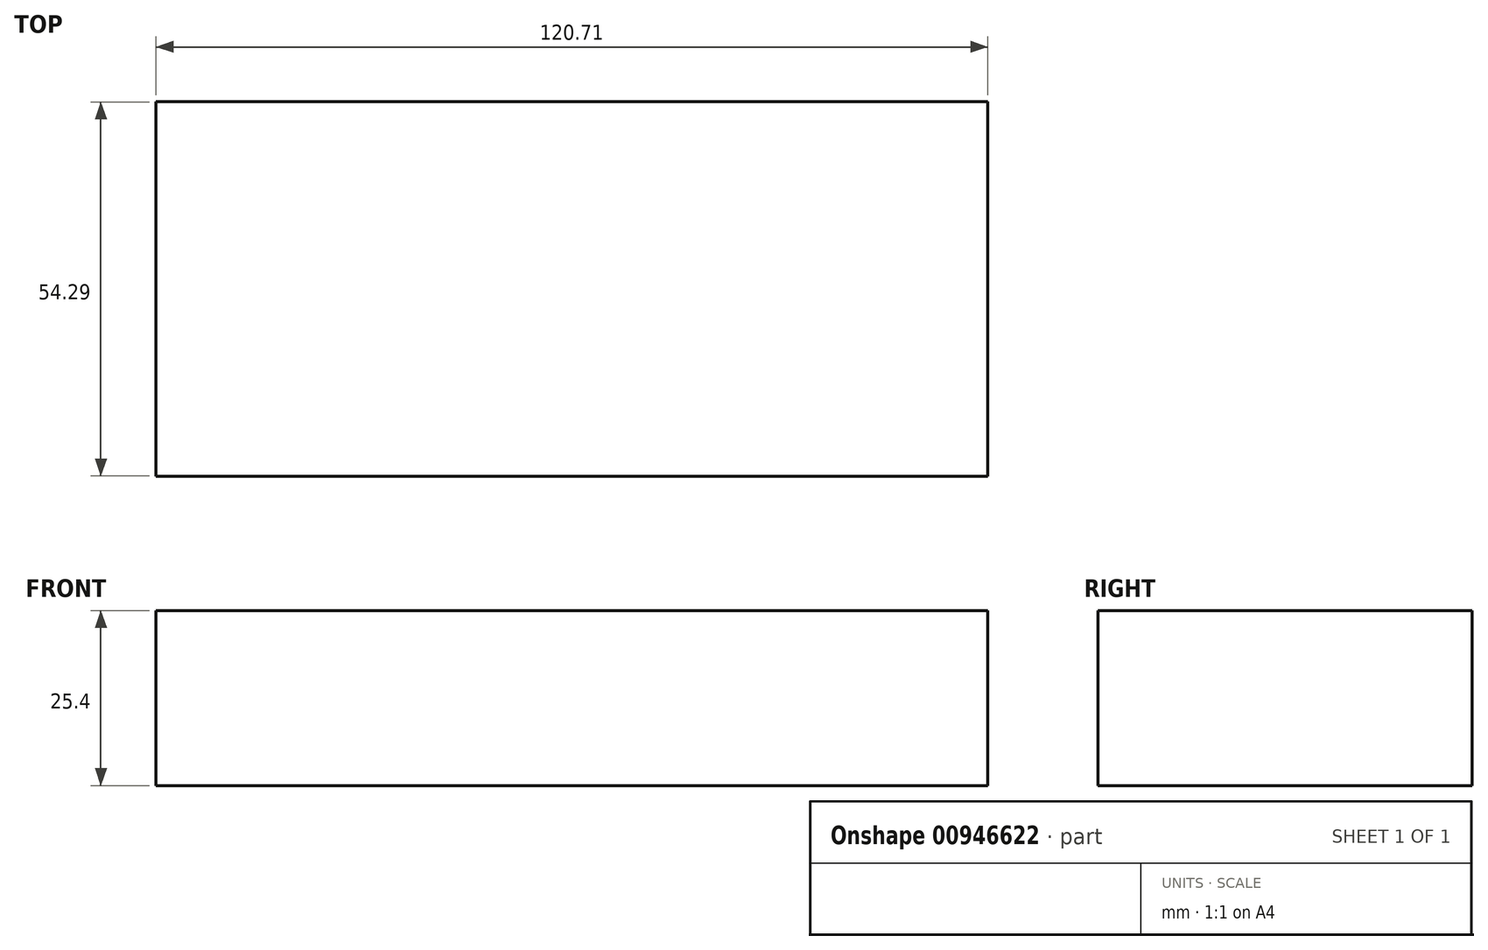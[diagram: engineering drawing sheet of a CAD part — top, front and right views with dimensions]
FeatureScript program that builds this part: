
annotation { "Feature Type Name" : "Feature", "Feature Type Description" : "" }
export const myFeature = defineFeature(function(context is Context, id is Id, definition is map)
    precondition{}
    {
        {
            var Q0;
            Q0=qCreatedBy(makeId("Top.planeOp"),FACE);
            var sketch = newSketch(context, id + "F0", { "sketchPlane" : qUnion([Q0])});
            skLineSegment(sketch, "E0.bottom", {"start": v(-60.23, 22.93) * mm, "end": v(60.48, 22.93) * mm});
            skLineSegment(sketch, "E0.top", {"start": v(-60.23, -31.36) * mm, "end": v(60.48, -31.36) * mm});
            skLineSegment(sketch, "E0.left", {"start": v(-60.23, 22.93) * mm, "end": v(-60.23, -31.36) * mm});
            skLineSegment(sketch, "E0.right", {"start": v(60.48, 22.93) * mm, "end": v(60.48, -31.36) * mm});
            skSolve(sketch);
        }
        {
            var Q0;
            Q0=makeQuery(id+"F0.imprint","IMPRINT",FACE,{"disambiguationData":[TD([[makeQuery(id+"F0.imprint","IMPRINT",EDGE,{"derivedFrom":sQuery(id+"F0.wireOp",EDGE,"E0.bottom")}),-1.0]])]});
            extrude(context, id + "F1", {"entities" : qUnion([Q0]), "depth" : 25.4 * mm, "offsetDistance" : 25.4 * mm});
        }
    });
